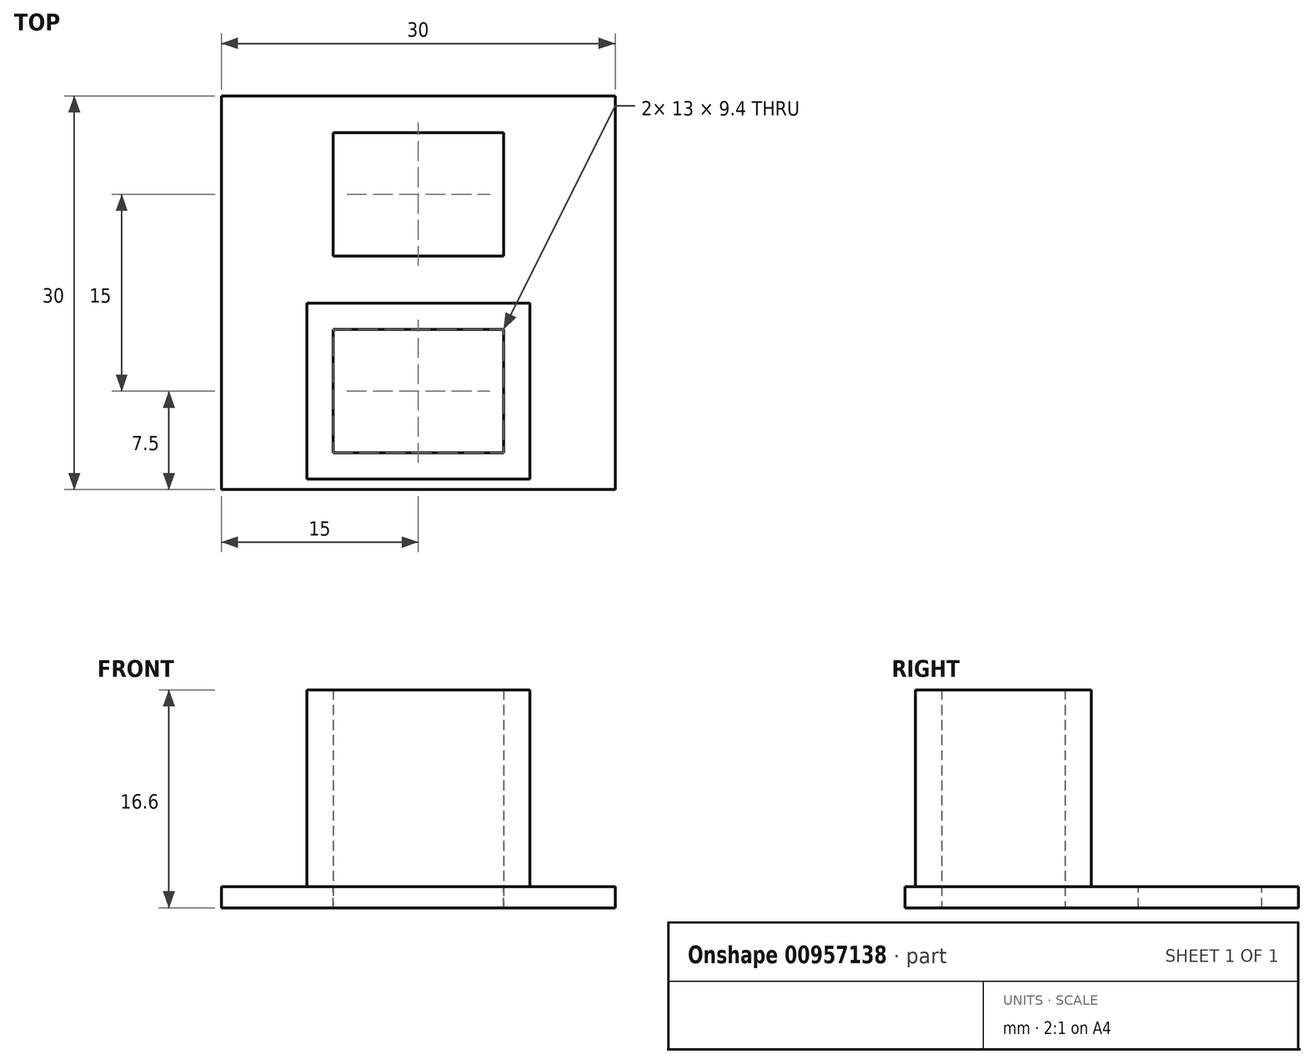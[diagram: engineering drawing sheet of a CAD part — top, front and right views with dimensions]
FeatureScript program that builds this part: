
annotation { "Feature Type Name" : "Feature", "Feature Type Description" : "" }
export const myFeature = defineFeature(function(context is Context, id is Id, definition is map)
    precondition{}
    {
        {
            var Q0;
            Q0=qCreatedBy(makeId("Top.planeOp"),FACE);
            var sketch = newSketch(context, id + "F0", { "sketchPlane" : qUnion([Q0])});
            skLineSegment(sketch, "E0.bottom", {"start": v(0, 0) * mm, "end": v(30, 0) * mm});
            skLineSegment(sketch, "E0.top", {"start": v(0, -30) * mm, "end": v(30, -30) * mm});
            skLineSegment(sketch, "E0.left", {"start": v(0, 0) * mm, "end": v(0, -30) * mm});
            skLineSegment(sketch, "E0.right", {"start": v(30, 0) * mm, "end": v(30, -30) * mm});
            skSolve(sketch);
        }
        {
            var Q0;
            Q0=makeQuery(id+"F0.imprint","IMPRINT",FACE,{"disambiguationData":[TD([[makeQuery(id+"F0.imprint","IMPRINT",EDGE,{"derivedFrom":sQuery(id+"F0.wireOp",EDGE,"E0.bottom")}),-1.0]])]});
            extrude(context, id + "F1", {"entities" : qUnion([Q0]), "depth" : 1.6 * mm, "offsetDistance" : 25 * mm});
        }
        {
            var Q0;
            Q0=makeQuery(id+"F1.opExtrude","CAP_FACE",FACE,{"disambiguationData":[OSD([sQuery(id+"F0.wireOp",EDGE,"E0.bottom"),sQuery(id+"F0.wireOp",EDGE,"E0.top"),sQuery(id+"F0.wireOp",EDGE,"E0.left"),sQuery(id+"F0.wireOp",EDGE,"E0.right")])],"isStart":false});
            var sketch = newSketch(context, id + "F2", { "sketchPlane" : qUnion([Q0])});
            skLineSegment(sketch, "E1", {"start": v(0, -15) * mm, "end": v(30, -15) * mm});
            skLineSegment(sketch, "E2.0", {"start": v(8.5, -12.2) * mm, "end": v(21.5, -12.2) * mm});
            skLineSegment(sketch, "E3.0", {"start": v(8.5, -2.8) * mm, "end": v(21.5, -2.8) * mm});
            skLineSegment(sketch, "E4", {"start": v(8.5, -2.8) * mm, "end": v(8.5, -12.2) * mm});
            skLineSegment(sketch, "E5", {"start": v(21.5, -2.8) * mm, "end": v(21.5, -12.2) * mm});
            skLineSegment(sketch, "E6.bottom", {"start": v(8.5, -17.8) * mm, "end": v(21.5, -17.8) * mm});
            skLineSegment(sketch, "E6.top", {"start": v(8.5, -27.2) * mm, "end": v(21.5, -27.2) * mm});
            skLineSegment(sketch, "E6.left", {"start": v(8.5, -17.8) * mm, "end": v(8.5, -27.2) * mm});
            skLineSegment(sketch, "E6.right", {"start": v(21.5, -17.8) * mm, "end": v(21.5, -27.2) * mm});
            skLineSegment(sketch, "E7.0", {"start": v(23.5, -15.8) * mm, "end": v(23.5, -29.2) * mm});
            skLineSegment(sketch, "E7.1", {"start": v(6.5, -15.8) * mm, "end": v(23.5, -15.8) * mm});
            skLineSegment(sketch, "E7.2", {"start": v(6.5, -15.8) * mm, "end": v(6.5, -29.2) * mm});
            skLineSegment(sketch, "E7.3", {"start": v(6.5, -29.2) * mm, "end": v(23.5, -29.2) * mm});
            skSolve(sketch);
        }
        {
            var Q0;
            {var subQ0=sQuery(id+"F2.wireOp",EDGE,"E4");Q0=makeQuery(id+"F2.imprint","IMPRINT",FACE,{"disambiguationData":[TD([[makeQuery(id+"F2.imprint","IMPRINT",EDGE,{"derivedFrom":subQ0}),1.0]])]});}
            extrude(context, id + "F3", {"entities" : qUnion([Q0]), "operationType" : NewBodyOperationType.REMOVE, "oppositeDirection" : true, "depth" : 25 * mm, "offsetDistance" : 25 * mm});
        }
        {
            var Q0;
            Q0=makeQuery(id+"F2.imprint","IMPRINT",FACE,{"disambiguationData":[TD([[makeQuery(id+"F2.imprint","IMPRINT",EDGE,{"derivedFrom":sQuery(id+"F2.wireOp",EDGE,"E6.bottom")}),1.0]])]});
            extrude(context, id + "F4", {"entities" : qUnion([Q0]), "operationType" : NewBodyOperationType.ADD, "depth" : 15 * mm, "offsetDistance" : 25 * mm});
        }
        {
            var Q0;
            Q0=makeQuery(id+"F2.imprint","IMPRINT",FACE,{"disambiguationData":[TD([[makeQuery(id+"F2.imprint","IMPRINT",EDGE,{"derivedFrom":sQuery(id+"F2.wireOp",EDGE,"E6.bottom")}),-1.0]])]});
            extrude(context, id + "F5", {"entities" : qUnion([Q0]), "operationType" : NewBodyOperationType.REMOVE, "oppositeDirection" : true, "depth" : 25 * mm, "offsetDistance" : 25 * mm});
        }
    });
